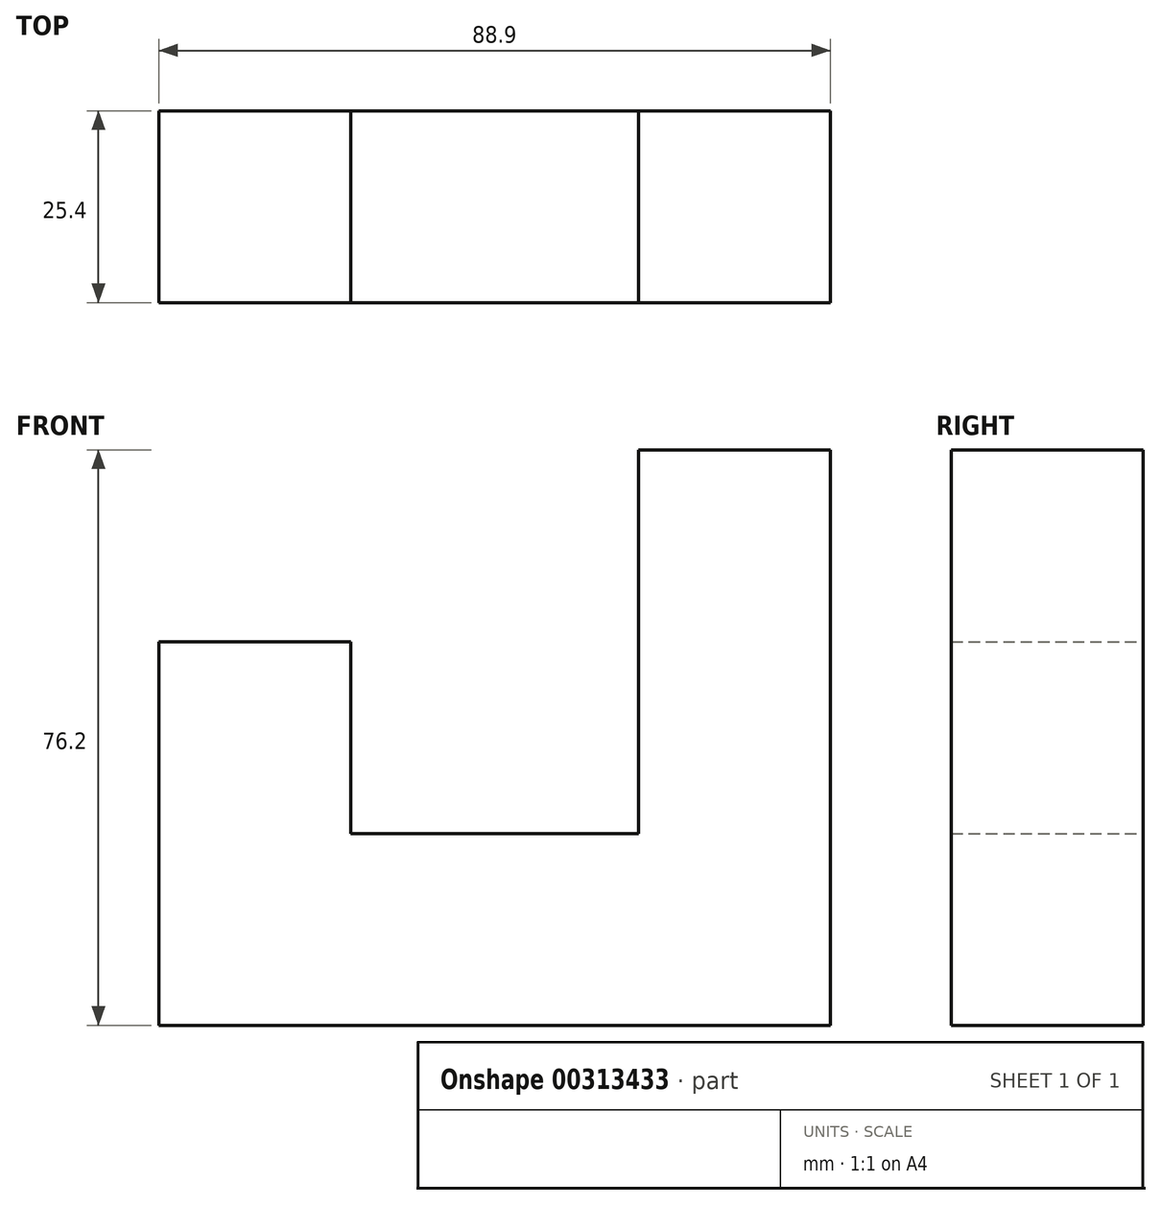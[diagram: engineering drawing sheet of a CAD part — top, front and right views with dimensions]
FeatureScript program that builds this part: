
annotation { "Feature Type Name" : "Feature", "Feature Type Description" : "" }
export const myFeature = defineFeature(function(context is Context, id is Id, definition is map)
    precondition{}
    {
        {
            var Q0;
            Q0=qCreatedBy(makeId("Front.planeOp"),FACE);
            var sketch = newSketch(context, id + "F0", { "sketchPlane" : qUnion([Q0])});
            skLineSegment(sketch, "E0", {"start": v(-46.5, -20.4) * mm, "end": v(42.4, -20.4) * mm});
            skLineSegment(sketch, "E1", {"start": v(42.4, -20.4) * mm, "end": v(42.4, 55.8) * mm});
            skLineSegment(sketch, "E2", {"start": v(42.4, 55.8) * mm, "end": v(17, 55.8) * mm});
            skLineSegment(sketch, "E3", {"start": v(17, 55.8) * mm, "end": v(17, 5) * mm});
            skLineSegment(sketch, "E4", {"start": v(17, 5) * mm, "end": v(-21.1, 5) * mm});
            skLineSegment(sketch, "E5", {"start": v(-21.1, 5) * mm, "end": v(-21.1, 30.4) * mm});
            skLineSegment(sketch, "E6", {"start": v(-21.1, 30.4) * mm, "end": v(-46.5, 30.4) * mm});
            skLineSegment(sketch, "E7", {"start": v(-46.5, 30.4) * mm, "end": v(-46.5, -20.4) * mm});
            skSolve(sketch);
        }
        {
            var Q0;
            Q0=makeQuery(id+"F0.imprint","IMPRINT",FACE,{"disambiguationData":[TD([[makeQuery(id+"F0.imprint","IMPRINT",EDGE,{"derivedFrom":sQuery(id+"F0.wireOp",EDGE,"E0")}),1.0]])]});
            extrude(context, id + "F1", {"entities" : qUnion([Q0]), "depth" : 25.4 * mm});
        }
    });
